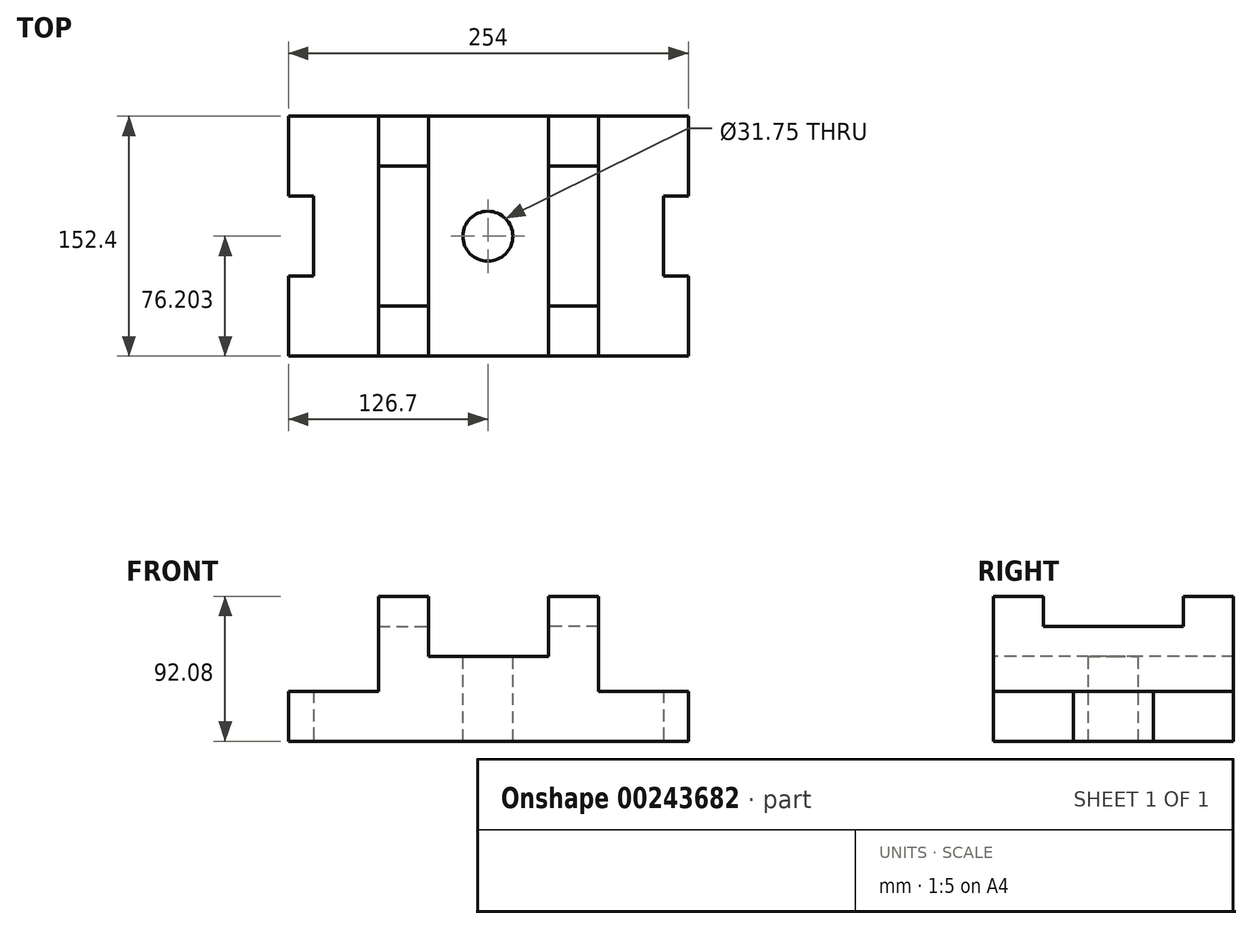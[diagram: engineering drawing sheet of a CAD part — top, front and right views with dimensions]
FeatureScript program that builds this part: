
annotation { "Feature Type Name" : "Feature", "Feature Type Description" : "" }
export const myFeature = defineFeature(function(context is Context, id is Id, definition is map)
    precondition{}
    {
        {
            var Q0;
            Q0=qCreatedBy(makeId("Top.planeOp"),FACE);
            var sketch = newSketch(context, id + "F0", { "sketchPlane" : qUnion([Q0])});
            skLineSegment(sketch, "E0.bottom", {"start": v(-118.3, 68.32) * mm, "end": v(-61.15, 68.32) * mm});
            skLineSegment(sketch, "E0.left", {"start": v(-118.3, 68.32) * mm, "end": v(-118.3, 17.52) * mm});
            skLineSegment(sketch, "E1.bottom", {"start": v(-118.3, 17.52) * mm, "end": v(-102.42, 17.52) * mm});
            skLineSegment(sketch, "E1.right", {"start": v(-102.42, 17.52) * mm, "end": v(-102.42, -7.88) * mm});
            skPoint(sketch, "E0.right.start.orphan", {"position": v(135.7, 68.32) * mm});
            skLineSegment(sketch, "E2", {"start": v(-61.15, 68.32) * mm, "end": v(-61.15, 36.57) * mm});
            skLineSegment(sketch, "E3", {"start": v(-29.4, 68.32) * mm, "end": v(-29.4, 36.57) * mm});
            skLineSegment(sketch, "E4", {"start": v(-61.15, 36.57) * mm, "end": v(-29.4, 36.57) * mm});
            skLineSegment(sketch, "E5", {"start": v(-61.15, 68.32) * mm, "end": v(-29.4, 68.32) * mm});
            skLineSegment(sketch, "E6", {"start": v(-29.4, 68.32) * mm, "end": v(8.7, 68.32) * mm});
            skLineSegment(sketch, "E7", {"start": v(-61.15, 36.57) * mm, "end": v(-61.15, -7.88) * mm});
            skLineSegment(sketch, "E8", {"start": v(-29.4, 36.57) * mm, "end": v(-29.4, 36.57) * mm});
            skLineSegment(sketch, "E9", {"start": v(-29.4, 36.57) * mm, "end": v(-29.4, -7.88) * mm});
            skLineSegment(sketch, "E10.MirrorCS", {"start": v(-118.3, -84.08) * mm, "end": v(-61.15, -84.08) * mm});
            skLineSegment(sketch, "E11.MirrorCS", {"start": v(-118.3, -84.08) * mm, "end": v(-118.3, -33.28) * mm});
            skLineSegment(sketch, "E12.MirrorCS", {"start": v(-29.4, -84.08) * mm, "end": v(-29.4, -52.33) * mm});
            skLineSegment(sketch, "E13.MirrorCS", {"start": v(-61.15, -84.08) * mm, "end": v(-61.15, -52.33) * mm});
            skLineSegment(sketch, "E14.MirrorCS", {"start": v(-61.15, -84.08) * mm, "end": v(-29.4, -84.08) * mm});
            skLineSegment(sketch, "E15.MirrorCS", {"start": v(-29.4, -52.33) * mm, "end": v(-29.4, -52.33) * mm});
            skLineSegment(sketch, "E16.MirrorCS", {"start": v(-29.4, -52.33) * mm, "end": v(-29.4, -7.88) * mm});
            skLineSegment(sketch, "E17.MirrorCS", {"start": v(-61.15, -52.33) * mm, "end": v(-61.15, -7.88) * mm});
            skLineSegment(sketch, "E18.MirrorCS", {"start": v(-118.3, -33.28) * mm, "end": v(-102.42, -33.28) * mm});
            skLineSegment(sketch, "E19.MirrorCS", {"start": v(-29.4, -84.08) * mm, "end": v(8.7, -84.08) * mm});
            skLineSegment(sketch, "E20.MirrorCS", {"start": v(-102.42, -33.28) * mm, "end": v(-102.42, -7.88) * mm});
            skLineSegment(sketch, "E21.MirrorCS", {"start": v(-61.15, -52.33) * mm, "end": v(-29.4, -52.33) * mm});
            skLineSegment(sketch, "E22.MirrorCS", {"start": v(46.8, 68.32) * mm, "end": v(8.7, 68.32) * mm});
            skLineSegment(sketch, "E23.MirrorCS", {"start": v(46.8, 68.32) * mm, "end": v(46.8, 36.57) * mm});
            skLineSegment(sketch, "E24.MirrorCS", {"start": v(78.55, 68.32) * mm, "end": v(46.8, 68.32) * mm});
            skLineSegment(sketch, "E25.MirrorCS", {"start": v(78.55, 68.32) * mm, "end": v(78.55, 36.57) * mm});
            skLineSegment(sketch, "E26.MirrorCS", {"start": v(78.55, 36.57) * mm, "end": v(78.55, -7.88) * mm});
            skLineSegment(sketch, "E27.MirrorCS", {"start": v(46.8, 36.57) * mm, "end": v(46.8, -7.88) * mm});
            skLineSegment(sketch, "E28.MirrorCS", {"start": v(78.55, 36.57) * mm, "end": v(46.8, 36.57) * mm});
            skLineSegment(sketch, "E29.MirrorCS", {"start": v(135.7, 68.32) * mm, "end": v(78.55, 68.32) * mm});
            skLineSegment(sketch, "E30.MirrorCS", {"start": v(135.7, 68.32) * mm, "end": v(135.7, 17.52) * mm});
            skLineSegment(sketch, "E31.MirrorCS", {"start": v(119.83, 17.52) * mm, "end": v(119.83, -7.88) * mm});
            skLineSegment(sketch, "E32.MirrorCS", {"start": v(135.7, 17.52) * mm, "end": v(119.83, 17.52) * mm});
            skLineSegment(sketch, "E33.MirrorCS", {"start": v(78.55, -52.33) * mm, "end": v(46.8, -52.33) * mm});
            skLineSegment(sketch, "E34.MirrorCS", {"start": v(135.7, -33.28) * mm, "end": v(119.83, -33.28) * mm});
            skLineSegment(sketch, "E35.MirrorCS", {"start": v(119.83, -33.28) * mm, "end": v(119.83, -7.88) * mm});
            skLineSegment(sketch, "E36.MirrorCS", {"start": v(135.7, -84.08) * mm, "end": v(135.7, -33.28) * mm});
            skLineSegment(sketch, "E37.MirrorCS", {"start": v(135.7, -84.08) * mm, "end": v(78.55, -84.08) * mm});
            skLineSegment(sketch, "E38.MirrorCS", {"start": v(78.55, -84.08) * mm, "end": v(78.55, -52.33) * mm});
            skLineSegment(sketch, "E39.MirrorCS", {"start": v(78.55, -52.33) * mm, "end": v(78.55, -7.88) * mm});
            skLineSegment(sketch, "E40.MirrorCS", {"start": v(46.8, -52.33) * mm, "end": v(46.8, -7.88) * mm});
            skLineSegment(sketch, "E41.MirrorCS", {"start": v(46.8, -84.08) * mm, "end": v(46.8, -52.33) * mm});
            skLineSegment(sketch, "E42.MirrorCS", {"start": v(78.55, -84.08) * mm, "end": v(46.8, -84.08) * mm});
            skLineSegment(sketch, "E43.MirrorCS", {"start": v(46.8, -84.08) * mm, "end": v(8.7, -84.08) * mm});
            skPoint(sketch, "E44.orphan", {"position": v(8.7, -7.88) * mm});
            skPoint(sketch, "E45.MirrorCS.start.orphan", {"position": v(119.83, -7.88) * mm});
            skSolve(sketch);
        }
        {
            var Q0;
            Q0=makeQuery(id+"F0.imprint","IMPRINT",FACE,{"disambiguationData":[TD([[makeQuery(id+"F0.imprint","IMPRINT",EDGE,{"derivedFrom":sQuery(id+"F0.wireOp",EDGE,"E0.bottom")}),-1.0]])]});
            extrude(context, id + "F1", {"entities" : qUnion([Q0]), "depth" : 31.75 * mm});
        }
        {
            var Q0;
            Q0=makeQuery(id+"F0.imprint","IMPRINT",FACE,{"disambiguationData":[TD([[makeQuery(id+"F0.imprint","IMPRINT",EDGE,{"derivedFrom":sQuery(id+"F0.wireOp",EDGE,"E4")}),-1.0]])]});
            extrude(context, id + "F2", {"entities" : qUnion([Q0]), "operationType" : NewBodyOperationType.ADD, "depth" : 73.02 * mm});
        }
        {
            var Q0;
            Q0=makeQuery(id+"F0.imprint","IMPRINT",FACE,{"disambiguationData":[TD([[makeQuery(id+"F0.imprint","IMPRINT",EDGE,{"derivedFrom":sQuery(id+"F0.wireOp",EDGE,"E12.MirrorCS")}),1.0]])]});
            var Q1;
            Q1=makeQuery(id+"F0.imprint","IMPRINT",FACE,{"disambiguationData":[TD([[makeQuery(id+"F0.imprint","IMPRINT",EDGE,{"derivedFrom":sQuery(id+"F0.wireOp",EDGE,"E2")}),1.0]])]});
            extrude(context, id + "F3", {"entities" : qUnion([Q0, Q1]), "operationType" : NewBodyOperationType.ADD, "depth" : 92.07 * mm});
        }
        {
            var Q0;
            Q0=makeQuery(id+"F0.imprint","IMPRINT",FACE,{"disambiguationData":[TD([[makeQuery(id+"F0.imprint","IMPRINT",EDGE,{"derivedFrom":sQuery(id+"F0.wireOp",EDGE,"E3")}),1.0]])]});
            extrude(context, id + "F4", {"entities" : qUnion([Q0]), "operationType" : NewBodyOperationType.ADD, "depth" : 53.97 * mm});
        }
        {
            var Q0;
            Q0=makeQuery(id+"F0.imprint","IMPRINT",FACE,{"disambiguationData":[TD([[makeQuery(id+"F0.imprint","IMPRINT",EDGE,{"derivedFrom":sQuery(id+"F0.wireOp",EDGE,"E26.MirrorCS")}),-1.0]])]});
            extrude(context, id + "F5", {"entities" : qUnion([Q0]), "operationType" : NewBodyOperationType.ADD, "depth" : 73.02 * mm});
        }
        {
            var Q0;
            Q0=makeQuery(id+"F0.imprint","IMPRINT",FACE,{"disambiguationData":[TD([[makeQuery(id+"F0.imprint","IMPRINT",EDGE,{"derivedFrom":sQuery(id+"F0.wireOp",EDGE,"E38.MirrorCS")}),1.0]])]});
            var Q1;
            Q1=makeQuery(id+"F0.imprint","IMPRINT",FACE,{"disambiguationData":[TD([[makeQuery(id+"F0.imprint","IMPRINT",EDGE,{"derivedFrom":sQuery(id+"F0.wireOp",EDGE,"E23.MirrorCS")}),1.0]])]});
            extrude(context, id + "F6", {"entities" : qUnion([Q0, Q1]), "operationType" : NewBodyOperationType.ADD, "depth" : 92.07 * mm});
        }
        {
            var Q0;
            Q0=makeQuery(id+"F0.imprint","IMPRINT",FACE,{"disambiguationData":[TD([[makeQuery(id+"F0.imprint","IMPRINT",EDGE,{"derivedFrom":sQuery(id+"F0.wireOp",EDGE,"E25.MirrorCS")}),1.0]])]});
            extrude(context, id + "F7", {"entities" : qUnion([Q0]), "operationType" : NewBodyOperationType.ADD, "depth" : 31.75 * mm});
        }
        {
            var Q0;
            Q0=makeQuery(id+"F4.opExtrude","CAP_FACE",FACE,{"disambiguationData":[OSD([sQuery(id+"F0.wireOp",EDGE,"E3"),sQuery(id+"F0.wireOp",EDGE,"E6"),sQuery(id+"F0.wireOp",EDGE,"E9"),sQuery(id+"F0.wireOp",EDGE,"E12.MirrorCS"),sQuery(id+"F0.wireOp",EDGE,"E16.MirrorCS"),sQuery(id+"F0.wireOp",EDGE,"E19.MirrorCS"),sQuery(id+"F0.wireOp",EDGE,"E22.MirrorCS"),sQuery(id+"F0.wireOp",EDGE,"E23.MirrorCS"),sQuery(id+"F0.wireOp",EDGE,"E27.MirrorCS"),sQuery(id+"F0.wireOp",EDGE,"E40.MirrorCS"),sQuery(id+"F0.wireOp",EDGE,"E41.MirrorCS"),sQuery(id+"F0.wireOp",EDGE,"E43.MirrorCS")])],"isStart":false});
            var sketch = newSketch(context, id + "F8", { "sketchPlane" : qUnion([Q0])});
            skCircle(sketch, "E46", {"center": v(8.4, -7.88) * mm, "radius": 15.88 * mm});
            skSolve(sketch);
        }
        {
            var Q0;
            Q0=makeQuery(id+"F8.imprint","IMPRINT",FACE,{"disambiguationData":[TD([[makeQuery(id+"F8.imprint","IMPRINT",EDGE,{"derivedFrom":sQuery(id+"F8.wireOp",EDGE,"E46")}),1.0]])]});
            extrude(context, id + "F9", {"entities" : qUnion([Q0]), "operationType" : NewBodyOperationType.REMOVE, "oppositeDirection" : true, "depth" : 53.97 * mm});
        }
    });
